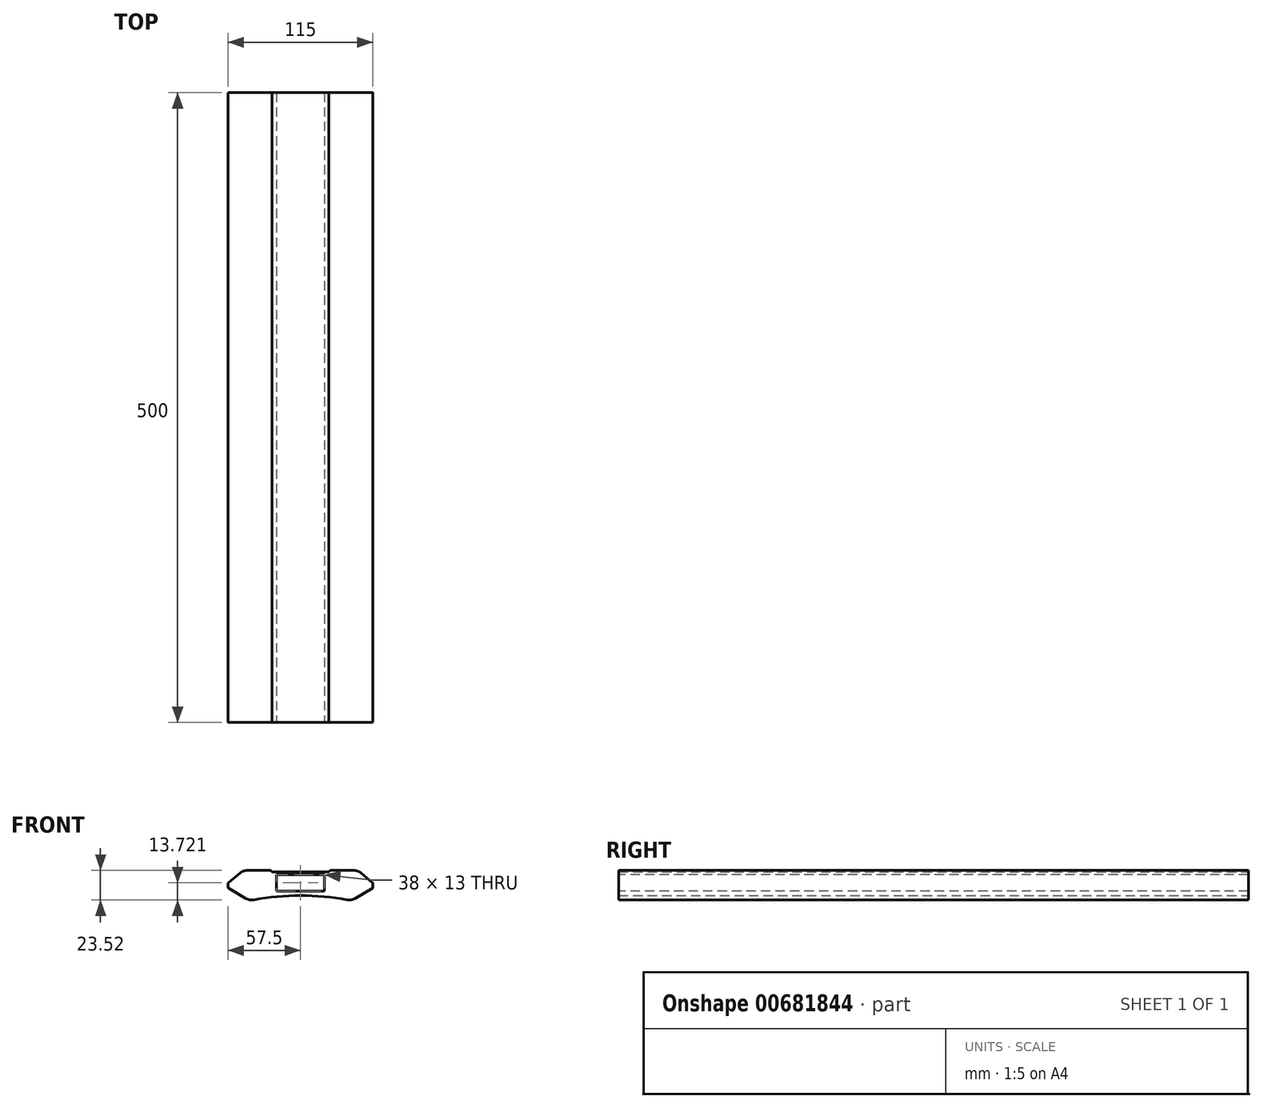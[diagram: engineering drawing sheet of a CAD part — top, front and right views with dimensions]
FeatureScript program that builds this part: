
annotation { "Feature Type Name" : "Feature", "Feature Type Description" : "" }
export const myFeature = defineFeature(function(context is Context, id is Id, definition is map)
    precondition{}
    {
        {
            var Q0;
            Q0=qCreatedBy(makeId("Front.planeOp"),FACE);
            var sketch = newSketch(context, id + "F0", { "sketchPlane" : qUnion([Q0])});
            skLineSegment(sketch, "E0", {"start": v(0, 0) * mm, "end": v(0, 46.3) * mm, "construction": true});
            skLineSegment(sketch, "E1", {"start": v(0, 23.15) * mm, "end": v(22.5, 23.15) * mm});
            skLineSegment(sketch, "E2", {"start": v(22.5, 23.15) * mm, "end": v(22.5, 24.45) * mm});
            skLineSegment(sketch, "E3", {"start": v(22.5, 24.45) * mm, "end": v(45.58, 24.45) * mm});
            skLineSegment(sketch, "E4", {"start": v(45.58, 24.45) * mm, "end": v(57.5, 14.45) * mm});
            skLineSegment(sketch, "E5", {"start": v(57.5, 14.45) * mm, "end": v(57.5, 10.45) * mm});
            skLineSegment(sketch, "E6", {"start": v(57.5, 10.45) * mm, "end": v(40.18, 0.45) * mm});
            skLineSegment(sketch, "E7.MirrorCS", {"start": v(0, 23.15) * mm, "end": v(-22.5, 23.15) * mm});
            skLineSegment(sketch, "E8.MirrorCS", {"start": v(-22.5, 24.45) * mm, "end": v(-45.58, 24.45) * mm});
            skLineSegment(sketch, "E9.MirrorCS", {"start": v(-45.58, 24.45) * mm, "end": v(-57.5, 14.45) * mm});
            skLineSegment(sketch, "E10.MirrorCS", {"start": v(-22.5, 23.15) * mm, "end": v(-22.5, 24.45) * mm});
            skLineSegment(sketch, "E11.MirrorCS", {"start": v(-57.5, 14.45) * mm, "end": v(-57.5, 10.45) * mm});
            skLineSegment(sketch, "E12.MirrorCS", {"start": v(-57.5, 10.45) * mm, "end": v(-40.18, 0.45) * mm});
            skArc(sketch, "E13", {"start": v(40.18, 0.45) * mm, "mid": v(0, 4.53) * mm, "end": v(-40.18, 0.45) * mm});
            skSolve(sketch);
        }
        {
            var Q0;
            Q0=qSketchRegion(id+"F0",true);
            extrude(context, id + "F1", {"entities" : qUnion([Q0]), "endBound" : BoundingType.SYMMETRIC, "depth" : 500 * mm, "offsetDistance" : 25 * mm});
        }
        {
            var Q0;
            Q0=qCreatedBy(makeId("Front.planeOp"),FACE);
            var sketch = newSketch(context, id + "F2", { "sketchPlane" : qUnion([Q0])});
            skLineSegment(sketch, "E14.bottom", {"start": v(-19, 21.15) * mm, "end": v(19, 21.15) * mm});
            skLineSegment(sketch, "E14.top", {"start": v(-19, 8.15) * mm, "end": v(19, 8.15) * mm});
            skLineSegment(sketch, "E14.left", {"start": v(-19, 21.15) * mm, "end": v(-19, 8.15) * mm});
            skLineSegment(sketch, "E14.right", {"start": v(19, 21.15) * mm, "end": v(19, 8.15) * mm});
            skSolve(sketch);
        }
        {
            var Q0;
            Q0=qSketchRegion(id+"F2",true);
            extrude(context, id + "F3", {"entities" : qUnion([Q0]), "operationType" : NewBodyOperationType.REMOVE, "endBound" : BoundingType.SYMMETRIC, "oppositeDirection" : true, "depth" : 500 * mm, "offsetDistance" : 25 * mm});
        }
        {
            var Q0;
            Q0=makeQuery(id+"F1.opExtrude","SWEPT_EDGE",EDGE,{"disambiguationData":[OSD([sQuery(id+"F0.wireOp",EDGE,"E8.MirrorCS"),sQuery(id+"F0.wireOp",EDGE,"E10.MirrorCS")])]});
            var Q1;
            Q1=makeQuery(id+"F1.opExtrude","SWEPT_EDGE",EDGE,{"disambiguationData":[OSD([sQuery(id+"F0.wireOp",EDGE,"E2"),sQuery(id+"F0.wireOp",EDGE,"E3")])]});
            fillet(context, id + "F4", {"entities" : qUnion([Q0, Q1]), "radius" : 2 * mm, "tangentPropagation" : true, "allowEdgeOverflow" : false});
        }
        {
            var Q0;
            Q0=makeQuery(id+"F1.opExtrude","SWEPT_EDGE",EDGE,{"disambiguationData":[OSD([sQuery(id+"F0.wireOp",EDGE,"E3"),sQuery(id+"F0.wireOp",EDGE,"E4")])]});
            var Q1;
            Q1=makeQuery(id+"F1.opExtrude","SWEPT_EDGE",EDGE,{"disambiguationData":[OSD([sQuery(id+"F0.wireOp",EDGE,"E6"),sQuery(id+"F0.wireOp",EDGE,"E13")])]});
            var Q2;
            Q2=makeQuery(id+"F1.opExtrude","SWEPT_EDGE",EDGE,{"disambiguationData":[OSD([sQuery(id+"F0.wireOp",EDGE,"E8.MirrorCS"),sQuery(id+"F0.wireOp",EDGE,"E9.MirrorCS")])]});
            var Q3;
            Q3=makeQuery(id+"F1.opExtrude","SWEPT_EDGE",EDGE,{"disambiguationData":[OSD([sQuery(id+"F0.wireOp",EDGE,"E12.MirrorCS"),sQuery(id+"F0.wireOp",EDGE,"E13")])]});
            fillet(context, id + "F5", {"entities" : qUnion([Q0, Q1, Q2, Q3]), "radius" : 9 * mm, "tangentPropagation" : true, "allowEdgeOverflow" : false});
        }
        {
            var Q0;
            Q0=makeQuery(id+"F1.opExtrude","SWEPT_EDGE",EDGE,{"disambiguationData":[OSD([sQuery(id+"F0.wireOp",EDGE,"E4"),sQuery(id+"F0.wireOp",EDGE,"E5")])]});
            var Q1;
            Q1=makeQuery(id+"F1.opExtrude","SWEPT_EDGE",EDGE,{"disambiguationData":[OSD([sQuery(id+"F0.wireOp",EDGE,"E5"),sQuery(id+"F0.wireOp",EDGE,"E6")])]});
            var Q2;
            Q2=makeQuery(id+"F1.opExtrude","SWEPT_EDGE",EDGE,{"disambiguationData":[OSD([sQuery(id+"F0.wireOp",EDGE,"E9.MirrorCS"),sQuery(id+"F0.wireOp",EDGE,"E11.MirrorCS")])]});
            var Q3;
            Q3=makeQuery(id+"F1.opExtrude","SWEPT_EDGE",EDGE,{"disambiguationData":[OSD([sQuery(id+"F0.wireOp",EDGE,"E11.MirrorCS"),sQuery(id+"F0.wireOp",EDGE,"E12.MirrorCS")])]});
            fillet(context, id + "F6", {"entities" : qUnion([Q0, Q1, Q2, Q3]), "radius" : 1 * mm, "tangentPropagation" : true, "allowEdgeOverflow" : false});
        }
    });
